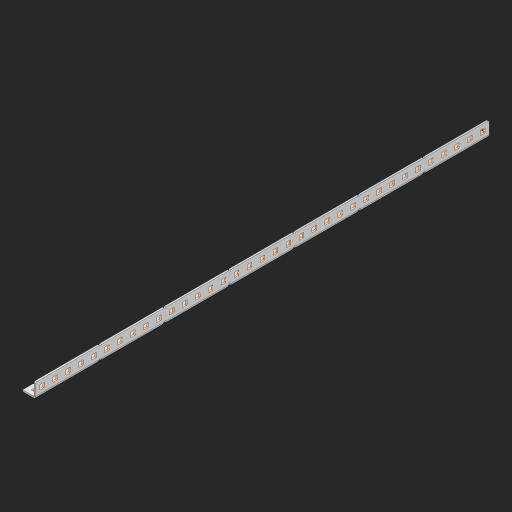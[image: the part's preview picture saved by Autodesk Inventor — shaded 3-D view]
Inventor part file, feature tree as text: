
AUTODESK INVENTOR PART (.ipt)
format: ipt  version: 2023 (Build 270158000, 158)  size: 1,368,064 bytes
history: native  units: in
note: dims shown in document units (in); Inventor stores cm internally (conversion verified against a paired STEP export)
features: other x252, extrude x102, sheet_metal_op x11, sketch x10, pattern_linear x2, mirror x1, chamfer x1
ambient origin geometry x8: Origin, YZ Plane, XZ Plane, XY Plane, X Axis, Y Axis, Z Axis, Center Point
bodies: Solid1 (feature_tree), Body (feature_tree)
feature tree (379):
  other  "Alu Half C 1x2x1x35"
  other  "Table"
  other  "Alu C 1x2x1x35"
  other  "Alu C 1x2x1x34"
  other  "Alu C 1x2x1x33"
  other  "Alu C 1x2x1x32"
  other  "Alu C 1x2x1x31"
  other  "Alu C 1x2x1x30"
  other  "Alu C 1x2x1x29"
  other  "Alu C 1x2x1x28"
  other  "Alu C 1x2x1x27"
  other  "Alu C 1x2x1x26"
  other  "Alu C 1x2x1x25"
  other  "Alu C 1x2x1x24"
  other  "Alu C 1x2x1x23"
  other  "Alu C 1x2x1x22"
  other  "Alu C 1x2x1x21"
  other  "Alu C 1x2x1x20"
  other  "Alu C 1x2x1x19"
  other  "Alu C 1x2x1x18"
  other  "Alu C 1x2x1x17"
  other  "Alu C 1x2x1x16"
  other  "Alu C 1x2x1x15"
  other  "Alu C 1x2x1x14"
  other  "Alu C 1x2x1x13"
  other  "Alu C 1x2x1x12"
  other  "Alu C 1x2x1x11"
  other  "Alu C 1x2x1x10"
  other  "Alu C 1x2x1x9"
  other  "Alu C 1x2x1x8"
  other  "Alu C 1x2x1x7"
  other  "Alu C 1x2x1x6"
  other  "Alu C 1x2x1x5"
  other  "Alu C 1x2x1x4"
  other  "Alu C 1x2x1x3"
  other  "Alu C 1x2x1x2"
  other  "Alu C 1x2x1x1"
  other  "Steel C 1x2x1x35"
  other  "Steel C 1x2x1x34"
  other  "Steel C 1x2x1x33"
  other  "Steel C 1x2x1x32"
  other  "Steel C 1x2x1x31"
  other  "Steel C 1x2x1x30"
  other  "Steel C 1x2x1x29"
  other  "Steel C 1x2x1x28"
  other  "Steel C 1x2x1x27"
  other  "Steel C 1x2x1x26"
  other  "Steel C 1x2x1x25"
  other  "Steel C 1x2x1x24"
  other  "Steel C 1x2x1x23"
  other  "Steel C 1x2x1x22"
  other  "Steel C 1x2x1x21"
  other  "Steel C 1x2x1x20"
  other  "Steel C 1x2x1x19"
  other  "Steel C 1x2x1x18"
  other  "Steel C 1x2x1x17"
  other  "Steel C 1x2x1x16"
  other  "Steel C 1x2x1x15"
  other  "Steel C 1x2x1x14"
  other  "Steel C 1x2x1x13"
  other  "Steel C 1x2x1x12"
  other  "Steel C 1x2x1x11"
  other  "Steel C 1x2x1x10"
  other  "Steel C 1x2x1x9"
  other  "Steel C 1x2x1x8"
  other  "Steel C 1x2x1x7"
  other  "Steel C 1x2x1x6"
  other  "Steel C 1x2x1x5"
  other  "Steel C 1x2x1x4"
  other  "Steel C 1x2x1x3"
  other  "Steel C 1x2x1x2"
  other  "Steel C 1x2x1x1"
  other  "Alu Half C 1x2x1x34"
  other  "Alu Half C 1x2x1x33"
  other  "Alu Half C 1x2x1x32"
  other  "Alu Half C 1x2x1x31"
  other  "Alu Half C 1x2x1x30"
  other  "Alu Half C 1x2x1x29"
  other  "Alu Half C 1x2x1x28"
  other  "Alu Half C 1x2x1x27"
  other  "Alu Half C 1x2x1x26"
  other  "Alu Half C 1x2x1x25"
  other  "Alu Half C 1x2x1x24"
  other  "Alu Half C 1x2x1x23"
  other  "Alu Half C 1x2x1x22"
  other  "Alu Half C 1x2x1x21"
  other  "Alu Half C 1x2x1x20"
  other  "Alu Half C 1x2x1x19"
  other  "Alu Half C 1x2x1x18"
  other  "Alu Half C 1x2x1x17"
  other  "Alu Half C 1x2x1x16"
  other  "Alu Half C 1x2x1x15"
  other  "Alu Half C 1x2x1x14"
  other  "Alu Half C 1x2x1x13"
  other  "Alu Half C 1x2x1x12"
  other  "Alu Half C 1x2x1x11"
  other  "Alu Half C 1x2x1x10"
  other  "Alu Half C 1x2x1x9"
  other  "Alu Half C 1x2x1x8"
  other  "Alu Half C 1x2x1x7"
  other  "Alu Half C 1x2x1x6"
  other  "Alu Half C 1x2x1x5"
  other  "Alu Half C 1x2x1x4"
  other  "Alu Half C 1x2x1x3"
  other  "Alu Half C 1x2x1x2"
  other  "Alu Half C 1x2x1x1"
  other  "Steel Half C 1x2x1x35"
  other  "Steel Half C 1x2x1x34"
  other  "Steel Half C 1x2x1x33"
  other  "Steel Half C 1x2x1x32"
  other  "Steel Half C 1x2x1x31"
  other  "Steel Half C 1x2x1x30"
  other  "Steel Half C 1x2x1x29"
  other  "Steel Half C 1x2x1x28"
  other  "Steel Half C 1x2x1x27"
  other  "Steel Half C 1x2x1x26"
  other  "Steel Half C 1x2x1x25"
  other  "Steel Half C 1x2x1x24"
  other  "Steel Half C 1x2x1x23"
  other  "Steel Half C 1x2x1x22"
  other  "Steel Half C 1x2x1x21"
  other  "Steel Half C 1x2x1x20"
  other  "Steel Half C 1x2x1x19"
  other  "Steel Half C 1x2x1x18"
  other  "Steel Half C 1x2x1x17"
  other  "Steel Half C 1x2x1x16"
  other  "Steel Half C 1x2x1x15"
  other  "Steel Half C 1x2x1x14"
  other  "Steel Half C 1x2x1x13"
  other  "Steel Half C 1x2x1x12"
  other  "Steel Half C 1x2x1x11"
  other  "Steel Half C 1x2x1x10"
  other  "Steel Half C 1x2x1x9"
  other  "Steel Half C 1x2x1x8"
  other  "Steel Half C 1x2x1x7"
  other  "Steel Half C 1x2x1x6"
  other  "Steel Half C 1x2x1x5"
  other  "Steel Half C 1x2x1x4"
  other  "Steel Half C 1x2x1x3"
  other  "Steel Half C 1x2x1x2"
  other  "Steel Half C 1x2x1x1"
  sheet_metal_op  "Flanges"
  other  "Flange Pattern Plane"
  other  "Flange Pattern Sketch"
  sheet_metal_op  "Flange Pattern"
  sheet_metal_op  "Body Pattern"
  pattern_linear  "Center Pattern"  Spacing1=0.0625in  [1 undecoded]
  other  "Arc Length"
  mirror  "Notch Mirror"
  pattern_linear  "Notch Pattern"  Spacing1=0.182in  [1 undecoded]
  chamfer  "End Chamfer"
  extrude  "Half Cut"  Depth=0.02in
  sketch  "Sketch1"  dims[d0=1.0in]
  other  "Plate1"
  sketch  "Sketch2"  dims[d1=17.5in]
  other  "Plate2"
  sheet_metal_op  "Bend1"
  sheet_metal_op  "Corner1"
  sketch  "Sketch3"  dims[d2=0.0625in]
  sketch  "Sketch7"  dims[d3=0.0625in]
  other  "Srf1"
  other  "Srf2"
  sketch  "Sketch8"  dims[d4=0.0312in]
  sketch  "Sketch9"  dims[d5=0.125in]
  other  "Srf91"
  sheet_metal_op  "Body Pattern Sketch"
  other  "Srf92"
  sketch  "Sketch13"  dims[d6=0.0625in]
  sketch  "Sketch14"  dims[d7=0.5in d8=90.0deg d9=0.0312in]
  sketch  "Sketch15"  dims[d10=0.25in]
  sketch  "Sketch16"  dims[d11=0.0625in d12=0.0625in d16=0.182in d17=0.02in d18=0.0625in d19=0.0in d20=0.25in d21=0.25in d38=13.7795in d40=0.5in d41=0.3937in d43=1.0in d46=0.172in d47=1.0in d48=0.0in d49=0.182in d50=0.02in d51=0.25in d52=0.25in d53=0.0625in d54=0.0in d55=0.172in d56=1.0in d57=0.0in d58=0.25in d60=13.7795in d62=0.5in d63=0.3937in d65=0.5in d85=0.1473in d86=0.1782in d88=0.04in d89=0.0625in d90=0.0in d91=0.04in d92=0.0491in d95=2.5in d96=0.04in d97=0.25in d98=45.0deg d99=0.25in d100=0.5in d101=0.0in d102=2.497in d106=0.182in d107=0.02in d108=0.5in d109=0.5in d110=0.0625in d111=0.0in d112=0.172in d113=0.5in d114=0.0in d117=0.5in d118=0.5in d119=0.5in]
  other  "Srf786"
  other  "Srf823"
  other  "Srf824"
  other  "Srf825"
  other  "Srf826"
  other  "Srf827"
  other  "Srf828"
  other  "Srf829"
  other  "Srf856"
  other  "Srf857"
  other  "Srf858"
  other  "Srf859"
  other  "Srf860"
  other  "Srf861"
  other  "Srf862"
  other  "Srf889"
  other  "Srf890"
  other  "Srf891"
  other  "Srf892"
  other  "Srf893"
  other  "Srf894"
  other  "Srf895"
  other  "Srf896"
  other  "Srf1275"
  other  "Srf1276"
  other  "Srf1277"
  other  "Srf1278"
  other  "Srf1279"
  other  "Srf1280"
  other  "Srf1281"
  other  "Srf1282"
  other  "Srf1283"
  other  "Srf1284"
  other  "Srf1285"
  other  "Srf1286"
  other  "Srf1287"
  other  "Srf1288"
  other  "Srf1289"
  other  "Srf1290"
  other  "Srf1291"
  other  "Srf1292"
  other  "Srf1293"
  other  "Srf1294"
  other  "Srf1295"
  other  "Srf1296"
  other  "Srf1297"
  other  "Srf1298"
  other  "Srf1299"
  other  "Srf1300"
  other  "Srf1301"
  other  "Srf1302"
  other  "Srf1303"
  other  "Srf1304"
  other  "Srf1305"
  other  "Srf1306"
  other  "Srf1307"
  other  "Srf1308"
  other  "Srf1309"
  other  "Srf1310"
  other  "Srf1311"
  other  "Srf1312"
  other  "Srf1313"
  other  "Srf1314"
  other  "Srf1315"
  other  "Srf1316"
  other  "Srf1317"
  other  "Srf1318"
  other  "Srf1319"
  other  "Srf1320"
  other  "Srf1321"
  other  "Srf1322"
  other  "Srf1323"
  other  "Srf1324"
  other  "Srf1325"
  other  "Srf1326"
  other  "Srf1327"
  other  "Srf1328"
  other  "Srf1329"
  other  "Srf1330"
  other  "Srf1331"
  other  "Srf1332"
  other  "Srf1333"
  other  "Srf1334"
  other  "Srf1335"
  other  "Srf1336"
  other  "Srf1337"
  other  "Srf1338"
  other  "Srf1339"
  other  "Srf1340"
  other  "Srf1341"
  other  "Srf1342"
  other  "Srf1343"
  other  "Srf1344"
  other  "Srf1345"
  other  "Srf1346"
  other  "Srf1347"
  other  "Srf1348"
  other  "Srf1349"
  other  "Srf1350"
  other  "Srf1351"
  sheet_metal_op  "Flange Stamp"
  sheet_metal_op  "Flange Circle"
  sheet_metal_op  "Body Stamp"
  sheet_metal_op  "Body Circle"
  other  "Center Stamp"
  other  "Center Circle"
  sheet_metal_op  "Notch"
  extrude  "ExtrusionSrf2"  Depth=0.0625in
  extrude  "ExtrusionSrf92"  TaperAngle=0.0deg  [1 undecoded]
  extrude  "ExtrusionSrf823"  Depth=0.25in
  extrude  "ExtrusionSrf824"  Depth=0.25in
  extrude  "ExtrusionSrf825"  Depth=0.5in
  extrude  "ExtrusionSrf826"  Depth=0.5in
  extrude  "ExtrusionSrf827"  Depth=1.0in TaperAngle=0.0deg
  extrude  "ExtrusionSrf828"  Depth=0.182in
  extrude  "ExtrusionSrf829"  Depth=0.02in
  extrude  "ExtrusionSrf856"  Depth=0.25in
  extrude  "ExtrusionSrf857"  Depth=0.25in
  extrude  "ExtrusionSrf858"  Depth=0.0625in
  extrude  "ExtrusionSrf859"  TaperAngle=0.0deg  [1 undecoded]
  extrude  "ExtrusionSrf860"  Depth=0.5in
  extrude  "ExtrusionSrf861"  Depth=1.0in TaperAngle=0.0deg
  extrude  "ExtrusionSrf862"  Depth=0.25in
  extrude  "ExtrusionSrf889"  Depth=0.5in
  extrude  "ExtrusionSrf890"  Depth=0.5in
  extrude  "ExtrusionSrf891"  Depth=0.5in
  extrude  "ExtrusionSrf892"  Depth=0.5in
  extrude  "ExtrusionSrf893"  Depth=0.5in
  extrude  "ExtrusionSrf894"  Depth=0.0625in
  extrude  "ExtrusionSrf895"  TaperAngle=0.0deg  [1 undecoded]
  extrude  "ExtrusionSrf896"  Depth=0.5in
  extrude  "ExtrusionSrf1275"  Depth=0.5in
  extrude  "ExtrusionSrf1276"  Depth=2.5in
  extrude  "ExtrusionSrf1277"  Depth=0.25in TaperAngle=45.0deg
  extrude  "ExtrusionSrf1278"  Depth=0.25in
  extrude  "ExtrusionSrf1279"  Depth=0.5in TaperAngle=0.0deg
  extrude  "ExtrusionSrf1280"  Depth=0.5in
  extrude  "ExtrusionSrf1281"  Depth=0.182in
  extrude  "ExtrusionSrf1282"  Depth=0.02in
  extrude  "ExtrusionSrf1283"  Depth=0.5in
  extrude  "ExtrusionSrf1284"  Depth=0.5in
  extrude  "ExtrusionSrf1285"  Depth=0.0625in
  extrude  "ExtrusionSrf1286"  TaperAngle=0.0deg  [1 undecoded]
  extrude  "ExtrusionSrf1287"  Depth=0.5in
  extrude  "ExtrusionSrf1288"  Depth=0.5in TaperAngle=0.0deg
  extrude  "ExtrusionSrf1289"  Depth=0.5in
  extrude  "ExtrusionSrf1290"  Depth=0.5in
  extrude  "ExtrusionSrf1291"  Depth=0.5in
  extrude  "ExtrusionSrf1292"  [1 undecoded]
  extrude  "ExtrusionSrf1293"  [1 undecoded]
  extrude  "ExtrusionSrf1294"  [1 undecoded]
  extrude  "ExtrusionSrf1295"  [1 undecoded]
  extrude  "ExtrusionSrf1296"  [1 undecoded]
  extrude  "ExtrusionSrf1297"  [1 undecoded]
  extrude  "ExtrusionSrf1298"  [1 undecoded]
  extrude  "ExtrusionSrf1299"  [1 undecoded]
  extrude  "ExtrusionSrf1300"  [1 undecoded]
  extrude  "ExtrusionSrf1301"  [1 undecoded]
  extrude  "ExtrusionSrf1302"  [1 undecoded]
  extrude  "ExtrusionSrf1303"  [1 undecoded]
  extrude  "ExtrusionSrf1304"  [1 undecoded]
  extrude  "ExtrusionSrf1305"  [1 undecoded]
  extrude  "ExtrusionSrf1306"  [1 undecoded]
  extrude  "ExtrusionSrf1307"  [1 undecoded]
  extrude  "ExtrusionSrf1308"  [1 undecoded]
  extrude  "ExtrusionSrf1309"  [1 undecoded]
  extrude  "ExtrusionSrf1310"  [1 undecoded]
  extrude  "ExtrusionSrf1311"  [1 undecoded]
  extrude  "ExtrusionSrf1312"  [1 undecoded]
  extrude  "ExtrusionSrf1313"  [1 undecoded]
  extrude  "ExtrusionSrf1314"  [1 undecoded]
  extrude  "ExtrusionSrf1315"  [1 undecoded]
  extrude  "ExtrusionSrf1316"  [1 undecoded]
  extrude  "ExtrusionSrf1317"  [1 undecoded]
  extrude  "ExtrusionSrf1318"  [1 undecoded]
  extrude  "ExtrusionSrf1319"  [1 undecoded]
  extrude  "ExtrusionSrf1320"  [1 undecoded]
  extrude  "ExtrusionSrf1321"  [1 undecoded]
  extrude  "ExtrusionSrf1322"  [1 undecoded]
  extrude  "ExtrusionSrf1323"  [1 undecoded]
  extrude  "ExtrusionSrf1324"  [1 undecoded]
  extrude  "ExtrusionSrf1325"  [1 undecoded]
  extrude  "ExtrusionSrf1326"  [1 undecoded]
  extrude  "ExtrusionSrf1327"  [1 undecoded]
  extrude  "ExtrusionSrf1328"  [1 undecoded]
  extrude  "ExtrusionSrf1329"  [1 undecoded]
  extrude  "ExtrusionSrf1330"  [1 undecoded]
  extrude  "ExtrusionSrf1331"  [1 undecoded]
  extrude  "ExtrusionSrf1332"  [1 undecoded]
  extrude  "ExtrusionSrf1333"  [1 undecoded]
  extrude  "ExtrusionSrf1334"  [1 undecoded]
  extrude  "ExtrusionSrf1335"  [1 undecoded]
  extrude  "ExtrusionSrf1336"  [1 undecoded]
  extrude  "ExtrusionSrf1337"  [1 undecoded]
  extrude  "ExtrusionSrf1338"  [1 undecoded]
  extrude  "ExtrusionSrf1339"  [1 undecoded]
  extrude  "ExtrusionSrf1340"  [1 undecoded]
  extrude  "ExtrusionSrf1341"  [1 undecoded]
  extrude  "ExtrusionSrf1342"  [1 undecoded]
  extrude  "ExtrusionSrf1343"  [1 undecoded]
  extrude  "ExtrusionSrf1344"  [1 undecoded]
  extrude  "ExtrusionSrf1345"  [1 undecoded]
  extrude  "ExtrusionSrf1346"  [1 undecoded]
  extrude  "ExtrusionSrf1347"  [1 undecoded]
  extrude  "ExtrusionSrf1348"  [1 undecoded]
  extrude  "ExtrusionSrf1349"  [1 undecoded]
  extrude  "ExtrusionSrf1350"  [1 undecoded]
  extrude  "ExtrusionSrf1351"  [1 undecoded]
note: 66 required parameter values undecoded (feature->parameter linkage not recoverable at this tier; creation-order binding heuristic only, values carry confidence <= 0.55)
